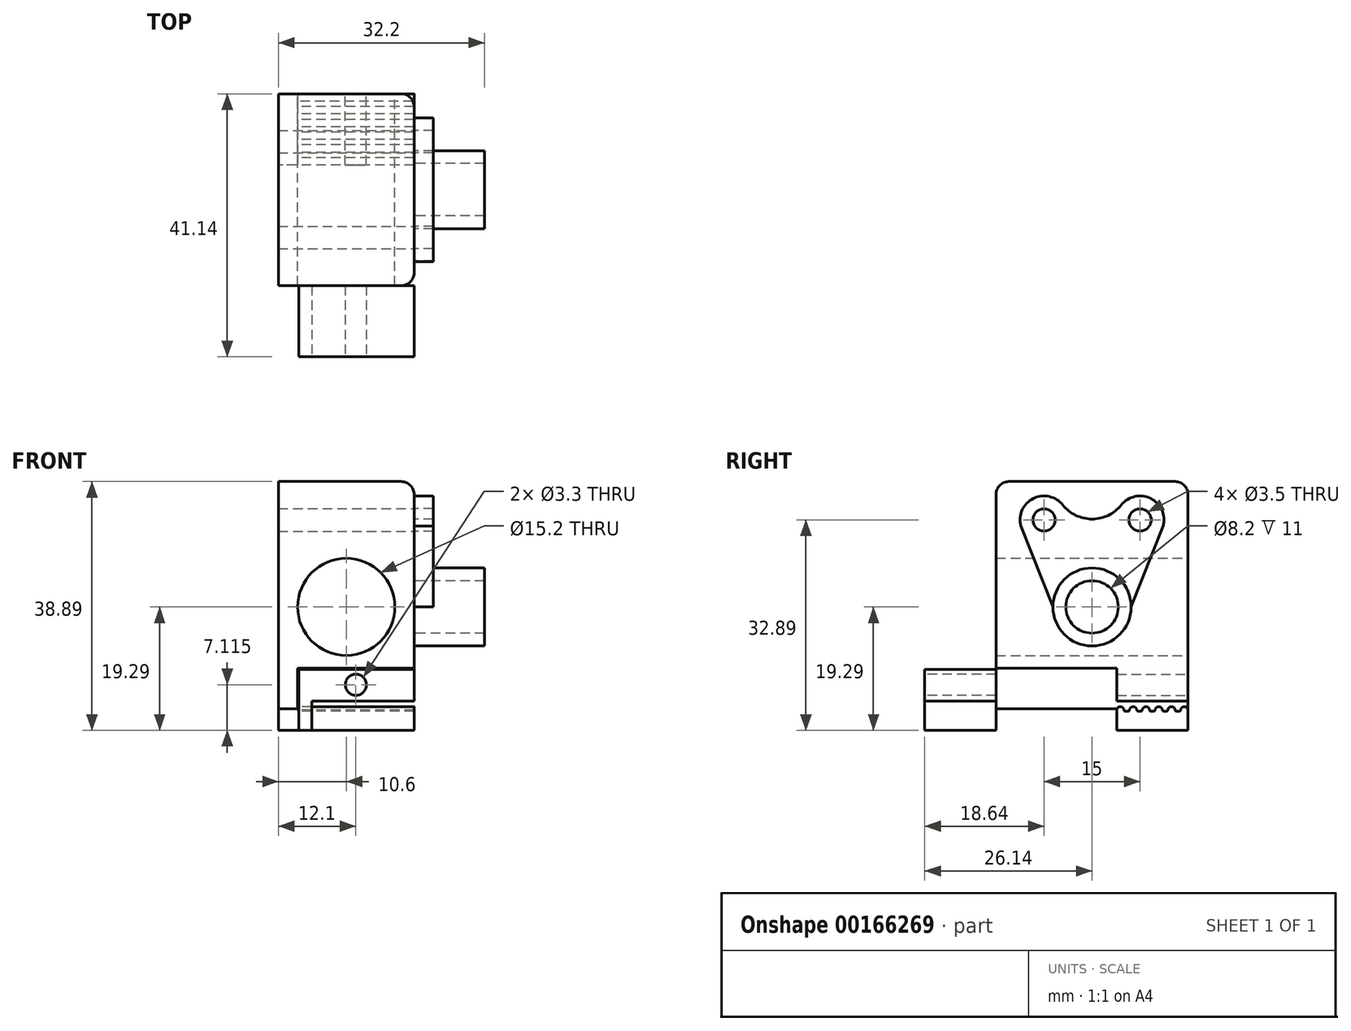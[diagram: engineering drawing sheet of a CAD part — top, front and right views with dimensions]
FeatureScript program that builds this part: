
annotation { "Feature Type Name" : "Feature", "Feature Type Description" : "" }
export const myFeature = defineFeature(function(context is Context, id is Id, definition is map)
    precondition{}
    {
        {
            var Q0;
            Q0=qCreatedBy(makeId("Front.planeOp"),FACE);
            var sketch = newSketch(context, id + "F0", { "sketchPlane" : qUnion([Q0])});
            skCircle(sketch, "E0", {"center": v(0, 0) * mm, "radius": 7.6 * mm});
            skLineSegment(sketch, "E1.bottom", {"start": v(-10.6, 19.6) * mm, "end": v(10.6, 19.6) * mm});
            skLineSegment(sketch, "E1.top", {"start": v(-10.6, -15.9) * mm, "end": v(-7.6, -15.9) * mm});
            skLineSegment(sketch, "E1.left", {"start": v(-10.6, 19.6) * mm, "end": v(-10.6, -15.9) * mm});
            skLineSegment(sketch, "E1.right", {"start": v(10.6, 19.6) * mm, "end": v(10.6, -9.6) * mm});
            skLineSegment(sketch, "E2", {"start": v(0, 0) * mm, "end": v(0, 19.6) * mm, "construction": true});
            skLineSegment(sketch, "E3", {"start": v(10.6, -9.6) * mm, "end": v(-7.6, -9.6) * mm});
            skLineSegment(sketch, "E4", {"start": v(-7.6, -9.6) * mm, "end": v(-7.6, -15.9) * mm});
            skLineSegment(sketch, "E5", {"start": v(-4.6, -10.75) * mm, "end": v(-4.6, -14.75) * mm});
            skLineSegment(sketch, "E6", {"start": v(-4.6, -14.75) * mm, "end": v(-7.6, -14.75) * mm});
            skLineSegment(sketch, "E7", {"start": v(-7.6, -12.75) * mm, "end": v(-10.6, -12.75) * mm, "construction": true});
            skLineSegment(sketch, "E8.MirrorCS", {"start": v(-4.6, -10.75) * mm, "end": v(-7.6, -10.75) * mm});
            skSolve(sketch);
        }
        {
            var Q0;
            Q0 = qSketchRegion(id + "F0", true);
            extrude(context, id + "F1", {"entities" : qUnion([Q0]), "depth" : 30 * mm});
        }
        {
            var Q0;
            {var subQ0=sQuery(id+"F0.wireOp",EDGE,"E4");Q0=makeQuery(id+"F1.opExtrude","SWEPT_FACE",FACE,{"disambiguationData":[OSD([subQ0]),TDD([makeQuery(id+"F0.imprint","IMPRINT",EDGE,{"disambiguationData":[TD([[makeQuery(id+"F0.imprint","INTERSECT",VERTEX,{"derivedFrom":[sQuery(id+"F0.wireOp",EDGE,"E3"),subQ0]}),-1.0]])],"derivedFrom":subQ0})])]});}
            var sketch = newSketch(context, id + "F2", { "sketchPlane" : qUnion([Q0])});
            skLineSegment(sketch, "E9.bottom", {"start": v(0, -9.6) * mm, "end": v(-11.14, -9.6) * mm});
            skLineSegment(sketch, "E9.top", {"start": v(-11.14, -12.6) * mm, "end": v(-30, -12.6) * mm, "construction": true});
            skLineSegment(sketch, "E9.left", {"start": v(0, -9.6) * mm, "end": v(0, -15.9) * mm});
            skLineSegment(sketch, "E9.right", {"start": v(-11.14, -9.6) * mm, "end": v(-11.14, -12.6) * mm});
            skLineSegment(sketch, "E10", {"start": v(-8.58, -12.6) * mm, "end": v(-8.58, -11.78) * mm, "construction": true});
            skArc(sketch, "E11", {"start": v(-8.08, -12.84) * mm, "mid": v(-8.58, -13.16) * mm, "end": v(-9.08, -12.84) * mm, "construction": true});
            skArc(sketch, "E12", {"start": v(-9.16, -12.6) * mm, "mid": v(-9.2, -12.5) * mm, "end": v(-9.31, -12.45) * mm, "construction": true});
            skArc(sketch, "E13", {"start": v(-9.08, -12.84) * mm, "mid": v(-9.13, -12.72) * mm, "end": v(-9.16, -12.6) * mm, "construction": true});
            skLineSegment(sketch, "E14", {"start": v(-8.58, -12.4) * mm, "end": v(-8.18, -12.4) * mm, "construction": true});
            skLineSegment(sketch, "E15", {"start": v(-9.58, -12.6) * mm, "end": v(-9.58, -11.78) * mm, "construction": true});
            skArc(sketch, "E16.MirrorCS", {"start": v(-11.14, -12.6) * mm, "mid": v(-10.7, -13.14) * mm, "end": v(-10.08, -12.84) * mm, "construction": true});
            skArc(sketch, "E17.MirrorCS", {"start": v(-10.08, -12.84) * mm, "mid": v(-10.03, -12.72) * mm, "end": v(-10, -12.6) * mm, "construction": true});
            skArc(sketch, "E18.MirrorCS", {"start": v(-10, -12.6) * mm, "mid": v(-9.96, -12.5) * mm, "end": v(-9.85, -12.45) * mm, "construction": true});
            skLineSegment(sketch, "E19", {"start": v(-9.31, -12.45) * mm, "end": v(-9.85, -12.45) * mm, "construction": true});
            skArc(sketch, "E20.MirrorCS", {"start": v(-8.08, -12.84) * mm, "mid": v(-8.03, -12.72) * mm, "end": v(-8, -12.6) * mm, "construction": true});
            skArc(sketch, "E21.MirrorCS", {"start": v(-7.08, -12.84) * mm, "mid": v(-7.13, -12.72) * mm, "end": v(-7.16, -12.6) * mm, "construction": true});
            skArc(sketch, "E22.MirrorCS", {"start": v(-7.16, -12.6) * mm, "mid": v(-7.2, -12.5) * mm, "end": v(-7.31, -12.45) * mm, "construction": true});
            skArc(sketch, "E23.MirrorCS", {"start": v(-8, -12.6) * mm, "mid": v(-7.96, -12.5) * mm, "end": v(-7.85, -12.45) * mm, "construction": true});
            skLineSegment(sketch, "E24.MirrorCS", {"start": v(-7.85, -12.45) * mm, "end": v(-7.31, -12.45) * mm, "construction": true});
            skArc(sketch, "E25.MirrorCS", {"start": v(-6.08, -12.84) * mm, "mid": v(-6.58, -13.16) * mm, "end": v(-7.08, -12.84) * mm, "construction": true});
            skLineSegment(sketch, "E26.0", {"start": v(-6.58, -16.97) * mm, "end": v(-6.58, -11.78) * mm, "construction": true});
            skArc(sketch, "E27.MirrorCS", {"start": v(-4.08, -12.84) * mm, "mid": v(-4.03, -12.72) * mm, "end": v(-4, -12.6) * mm, "construction": true});
            skArc(sketch, "E28.MirrorCS", {"start": v(-4, -12.6) * mm, "mid": v(-3.96, -12.5) * mm, "end": v(-3.85, -12.45) * mm, "construction": true});
            skArc(sketch, "E29.MirrorCS", {"start": v(-3.08, -12.84) * mm, "mid": v(-3.13, -12.72) * mm, "end": v(-3.16, -12.6) * mm, "construction": true});
            skArc(sketch, "E30.MirrorCS", {"start": v(-3.16, -12.6) * mm, "mid": v(-3.2, -12.5) * mm, "end": v(-3.31, -12.45) * mm, "construction": true});
            skArc(sketch, "E31.MirrorCS", {"start": v(-6, -12.6) * mm, "mid": v(-5.96, -12.5) * mm, "end": v(-5.85, -12.45) * mm, "construction": true});
            skArc(sketch, "E32.MirrorCS", {"start": v(-7.08, -12.84) * mm, "mid": v(-6.58, -13.16) * mm, "end": v(-6.08, -12.84) * mm, "construction": true});
            skArc(sketch, "E33.MirrorCS", {"start": v(-5.16, -12.6) * mm, "mid": v(-5.2, -12.5) * mm, "end": v(-5.31, -12.45) * mm, "construction": true});
            skArc(sketch, "E34.MirrorCS", {"start": v(-6.08, -12.84) * mm, "mid": v(-6.03, -12.72) * mm, "end": v(-6, -12.6) * mm, "construction": true});
            skArc(sketch, "E35.MirrorCS", {"start": v(-5.08, -12.84) * mm, "mid": v(-5.13, -12.72) * mm, "end": v(-5.16, -12.6) * mm, "construction": true});
            skArc(sketch, "E36.MirrorCS", {"start": v(-5.08, -12.84) * mm, "mid": v(-4.58, -13.16) * mm, "end": v(-4.08, -12.84) * mm, "construction": true});
            skArc(sketch, "E37.MirrorCS", {"start": v(-2.03, -12.6) * mm, "mid": v(-2.46, -13.14) * mm, "end": v(-3.08, -12.84) * mm, "construction": true});
            skLineSegment(sketch, "E38.MirrorCS", {"start": v(-5.31, -12.45) * mm, "end": v(-5.85, -12.45) * mm, "construction": true});
            skLineSegment(sketch, "E39.MirrorCS", {"start": v(-3.85, -12.45) * mm, "end": v(-3.31, -12.45) * mm, "construction": true});
            skLineSegment(sketch, "E40.MirrorCS", {"start": v(-2.03, -9.6) * mm, "end": v(-2.03, -12.6) * mm, "construction": true});
            skLineSegment(sketch, "E41.0", {"start": v(-2.58, -16.97) * mm, "end": v(-2.58, -11.78) * mm, "construction": true});
            skPoint(sketch, "E42.orphan", {"position": v(-8.03, -12.6) * mm});
            skPoint(sketch, "E43.orphan", {"position": v(-7.14, -12.6) * mm});
            skPoint(sketch, "E44.orphan", {"position": v(-6.03, -12.6) * mm});
            skPoint(sketch, "E45.orphan", {"position": v(-5.14, -12.6) * mm});
            skArc(sketch, "E46.MirrorCS", {"start": v(-2.08, -12.84) * mm, "mid": v(-2.03, -12.72) * mm, "end": v(-2, -12.6) * mm, "construction": true});
            skArc(sketch, "E47.MirrorCS", {"start": v(-2, -12.6) * mm, "mid": v(-1.96, -12.5) * mm, "end": v(-1.85, -12.45) * mm, "construction": true});
            skLineSegment(sketch, "E48.MirrorCS", {"start": v(-1.31, -12.45) * mm, "end": v(-1.85, -12.45) * mm, "construction": true});
            skArc(sketch, "E49.MirrorCS", {"start": v(-1.16, -12.6) * mm, "mid": v(-1.2, -12.5) * mm, "end": v(-1.31, -12.45) * mm, "construction": true});
            skArc(sketch, "E50.MirrorCS", {"start": v(-1.08, -12.84) * mm, "mid": v(-1.13, -12.72) * mm, "end": v(-1.16, -12.6) * mm, "construction": true});
            skArc(sketch, "E51.MirrorCS", {"start": v(-0.08, -12.84) * mm, "mid": v(-0.58, -13.16) * mm, "end": v(-1.08, -12.84) * mm, "construction": true});
            skArc(sketch, "E52.MirrorCS", {"start": v(-0.08, -12.84) * mm, "mid": v(-0.03, -12.72) * mm, "end": v(0, -12.6) * mm, "construction": true});
            skLineSegment(sketch, "E53", {"start": v(0, -12.6) * mm, "end": v(0, -9.6) * mm});
            skLineSegment(sketch, "E54", {"start": v(-2.58, -14.37) * mm, "end": v(-6.58, -14.37) * mm, "construction": true});
            skArc(sketch, "E55.MirrorCS", {"start": v(-2, -16.14) * mm, "mid": v(-1.96, -16.25) * mm, "end": v(-1.85, -16.3) * mm});
            skArc(sketch, "E56.MirrorCS", {"start": v(-7.08, -15.9) * mm, "mid": v(-7.13, -16.02) * mm, "end": v(-7.16, -16.14) * mm});
            skArc(sketch, "E57.MirrorCS", {"start": v(-7.16, -16.14) * mm, "mid": v(-7.2, -16.25) * mm, "end": v(-7.31, -16.3) * mm});
            skArc(sketch, "E58.MirrorCS", {"start": v(-6.08, -15.9) * mm, "mid": v(-6.03, -16.02) * mm, "end": v(-6, -16.14) * mm});
            skArc(sketch, "E59.MirrorCS", {"start": v(-5.16, -16.14) * mm, "mid": v(-5.2, -16.25) * mm, "end": v(-5.31, -16.3) * mm});
            skArc(sketch, "E60.MirrorCS", {"start": v(-6, -16.14) * mm, "mid": v(-5.96, -16.25) * mm, "end": v(-5.85, -16.3) * mm});
            skArc(sketch, "E61.MirrorCS", {"start": v(-8, -16.14) * mm, "mid": v(-7.96, -16.25) * mm, "end": v(-7.85, -16.3) * mm});
            skArc(sketch, "E62.MirrorCS", {"start": v(-10.08, -15.9) * mm, "mid": v(-10.03, -16.02) * mm, "end": v(-10, -16.14) * mm});
            skArc(sketch, "E63.MirrorCS", {"start": v(-10, -16.14) * mm, "mid": v(-9.96, -16.25) * mm, "end": v(-9.85, -16.3) * mm});
            skArc(sketch, "E64.MirrorCS", {"start": v(-9.08, -15.9) * mm, "mid": v(-9.13, -16.02) * mm, "end": v(-9.16, -16.14) * mm});
            skArc(sketch, "E65.MirrorCS", {"start": v(-8.08, -15.9) * mm, "mid": v(-8.03, -16.02) * mm, "end": v(-8, -16.14) * mm});
            skArc(sketch, "E66.MirrorCS", {"start": v(-3.16, -16.14) * mm, "mid": v(-3.2, -16.25) * mm, "end": v(-3.31, -16.3) * mm});
            skArc(sketch, "E67.MirrorCS", {"start": v(-1.08, -15.9) * mm, "mid": v(-1.13, -16.02) * mm, "end": v(-1.16, -16.14) * mm});
            skArc(sketch, "E68.MirrorCS", {"start": v(-5.08, -15.9) * mm, "mid": v(-5.13, -16.02) * mm, "end": v(-5.16, -16.14) * mm});
            skArc(sketch, "E69.MirrorCS", {"start": v(-1.16, -16.14) * mm, "mid": v(-1.2, -16.25) * mm, "end": v(-1.31, -16.3) * mm});
            skArc(sketch, "E70.MirrorCS", {"start": v(-4.08, -15.9) * mm, "mid": v(-4.03, -16.02) * mm, "end": v(-4, -16.14) * mm});
            skArc(sketch, "E71.MirrorCS", {"start": v(-9.16, -16.14) * mm, "mid": v(-9.2, -16.25) * mm, "end": v(-9.31, -16.3) * mm});
            skArc(sketch, "E72.MirrorCS", {"start": v(-3.08, -15.9) * mm, "mid": v(-3.13, -16.02) * mm, "end": v(-3.16, -16.14) * mm});
            skArc(sketch, "E73.MirrorCS", {"start": v(-4, -16.14) * mm, "mid": v(-3.96, -16.25) * mm, "end": v(-3.85, -16.3) * mm});
            skArc(sketch, "E74.MirrorCS", {"start": v(-0.08, -15.9) * mm, "mid": v(-0.03, -16.02) * mm, "end": v(0, -16.14) * mm});
            skLineSegment(sketch, "E75.MirrorCS", {"start": v(-9.31, -16.3) * mm, "end": v(-9.85, -16.3) * mm});
            skArc(sketch, "E76.MirrorCS", {"start": v(-2.08, -15.9) * mm, "mid": v(-2.03, -16.02) * mm, "end": v(-2, -16.14) * mm});
            skArc(sketch, "E77.MirrorCS", {"start": v(-2.03, -16.14) * mm, "mid": v(-2.46, -15.6) * mm, "end": v(-3.08, -15.9) * mm});
            skLineSegment(sketch, "E78.MirrorCS", {"start": v(-7.85, -16.3) * mm, "end": v(-7.31, -16.3) * mm});
            skPoint(sketch, "E79.MirrorP", {"position": v(-6.03, -16.14) * mm});
            skLineSegment(sketch, "E80.MirrorCS", {"start": v(-5.31, -16.3) * mm, "end": v(-5.85, -16.3) * mm});
            skArc(sketch, "E81.MirrorCS", {"start": v(-5.08, -15.9) * mm, "mid": v(-4.58, -15.59) * mm, "end": v(-4.08, -15.9) * mm});
            skPoint(sketch, "E82.MirrorP", {"position": v(-7.14, -16.14) * mm});
            skArc(sketch, "E83.MirrorCS", {"start": v(-8.08, -15.9) * mm, "mid": v(-8.58, -15.59) * mm, "end": v(-9.08, -15.9) * mm});
            skLineSegment(sketch, "E84.MirrorCS", {"start": v(-1.31, -16.3) * mm, "end": v(-1.85, -16.3) * mm});
            skArc(sketch, "E85.MirrorCS", {"start": v(-6.08, -15.9) * mm, "mid": v(-6.58, -15.59) * mm, "end": v(-7.08, -15.9) * mm});
            skPoint(sketch, "E86.MirrorP", {"position": v(-8.03, -16.14) * mm});
            skArc(sketch, "E87.MirrorCS", {"start": v(-7.08, -15.9) * mm, "mid": v(-6.58, -15.59) * mm, "end": v(-6.08, -15.9) * mm});
            skArc(sketch, "E88.MirrorCS", {"start": v(-0.08, -15.9) * mm, "mid": v(-0.58, -15.59) * mm, "end": v(-1.08, -15.9) * mm});
            skArc(sketch, "E89.MirrorCS", {"start": v(-11.14, -16.14) * mm, "mid": v(-10.7, -15.6) * mm, "end": v(-10.08, -15.9) * mm});
            skLineSegment(sketch, "E90.MirrorCS", {"start": v(-3.85, -16.3) * mm, "end": v(-3.31, -16.3) * mm});
            skPoint(sketch, "E91.MirrorP", {"position": v(-5.14, -16.14) * mm});
            skLineSegment(sketch, "E92", {"start": v(-11.14, -16.14) * mm, "end": v(-11.14, -19.3) * mm});
            skLineSegment(sketch, "E93", {"start": v(-11.14, -19.3) * mm, "end": v(0, -19.3) * mm});
            skLineSegment(sketch, "E94", {"start": v(0, -19.3) * mm, "end": v(0, -16.14) * mm});
            skLineSegment(sketch, "E95", {"start": v(0, -12.6) * mm, "end": v(0, -14.09) * mm});
            skLineSegment(sketch, "E96", {"start": v(0, -14.09) * mm, "end": v(-11.14, -14.09) * mm});
            skLineSegment(sketch, "E97", {"start": v(-11.14, -14.09) * mm, "end": v(-11.14, -12.6) * mm});
            skSolve(sketch);
        }
        {
            var Q0;
            {var subQ0=sQuery(id+"F2.wireOp",EDGE,"E9.bottom");Q0=makeQuery(id+"F2.imprint","IMPRINT",FACE,{"disambiguationData":[TD([[makeQuery(id+"F2.imprint","IMPRINT",EDGE,{"derivedFrom":subQ0}),-1.0]])]});}
            var Q1;
            Q1=makeQuery(id+"F2.imprint","IMPRINT",FACE,{"disambiguationData":[TD([[makeQuery(id+"F2.imprint","IMPRINT",EDGE,{"derivedFrom":sQuery(id+"F2.wireOp",EDGE,"E11")}),-1.0]])]});
            var Q2;
            Q2=makeQuery(id+"F1.opExtrude","SWEPT_FACE",FACE,{"disambiguationData":[OSD([sQuery(id+"F0.wireOp",EDGE,"E5")])]});
            var Q3;
            Q3=makeQuery(id+"F2.imprint","IMPRINT",FACE,{"disambiguationData":[TD([[makeQuery(id+"F2.imprint","IMPRINT",EDGE,{"derivedFrom":sQuery(id+"F2.wireOp",EDGE,"E55.MirrorCS")}),-1.0]])]});
            var Q4;
            Q4=makeQuery(id+"F1.opExtrude","SWEPT_FACE",FACE,{"disambiguationData":[OSD([sQuery(id+"F0.wireOp",EDGE,"E1.right")])]});
            extrude(context, id + "F3", {"entities" : qUnion([Q0, Q1, Q2, Q3]), "operationType" : NewBodyOperationType.ADD, "endBound" : BoundingType.UP_TO_SURFACE, "endBoundEntityFace" : qUnion([Q4]), "depth" : 25 * mm});
        }
        {
            var Q0;
            {var subQ0=sQuery(id+"F0.wireOp",EDGE,"E5");Q0=makeQuery(id+"F3.boolean.opBoolean","MERGE",FACE,{"derivedFrom":[makeQuery(id+"F1.opExtrude","CAP_FACE",FACE,{"disambiguationData":[OSD([sQuery(id+"F0.wireOp",EDGE,"E0"),sQuery(id+"F0.wireOp",EDGE,"E1.bottom"),sQuery(id+"F0.wireOp",EDGE,"E1.top"),sQuery(id+"F0.wireOp",EDGE,"E1.left"),sQuery(id+"F0.wireOp",EDGE,"E1.right"),sQuery(id+"F0.wireOp",EDGE,"E3"),sQuery(id+"F0.wireOp",EDGE,"E4"),subQ0,sQuery(id+"F0.wireOp",EDGE,"E6"),sQuery(id+"F0.wireOp",EDGE,"E8.MirrorCS")])],"isStart":true}),makeQuery(id+"F3.opExtrude","SWEPT_FACE",FACE,{"disambiguationData":[OSD([subQ0]),TDD([makeQuery(id+"F1.opExtrude","CAP_EDGE",EDGE,{"disambiguationData":[OSD([subQ0])],"isStart":true})])]}),makeQuery(id+"F3.opExtrude","SWEPT_FACE",FACE,{"disambiguationData":[OSD([sQuery(id+"F2.wireOp",EDGE,"E53")])]})]});}
            var sketch = newSketch(context, id + "F4", { "sketchPlane" : qUnion([Q0])});
            skLineSegment(sketch, "E98.bottom", {"start": v(10.6, -15.9) * mm, "end": v(7.6, -15.9) * mm});
            skLineSegment(sketch, "E98.top", {"start": v(10.6, -19.3) * mm, "end": v(7.6, -19.3) * mm});
            skLineSegment(sketch, "E98.left", {"start": v(10.6, -15.9) * mm, "end": v(10.6, -19.3) * mm});
            skLineSegment(sketch, "E98.right", {"start": v(7.6, -15.9) * mm, "end": v(7.6, -19.3) * mm});
            skSolve(sketch);
        }
        {
            var Q0;
            Q0=makeQuery(id+"F4.imprint","IMPRINT",FACE,{"disambiguationData":[TD([[makeQuery(id+"F4.imprint","IMPRINT",EDGE,{"derivedFrom":sQuery(id+"F4.wireOp",EDGE,"E98.bottom")}),1.0]])]});
            var Q1;
            Q1=makeQuery(id+"F3.opExtrude","SWEPT_FACE",FACE,{"disambiguationData":[OSD([sQuery(id+"F2.wireOp",EDGE,"E9.right")])]});
            extrude(context, id + "F5", {"entities" : qUnion([Q0]), "operationType" : NewBodyOperationType.ADD, "endBound" : BoundingType.UP_TO_SURFACE, "oppositeDirection" : true, "endBoundEntityFace" : qUnion([Q1]), "depth" : 25 * mm});
        }
        {
            var Q0;
            {var subQ0=sQuery(id+"F0.wireOp",EDGE,"E5");Q0=makeQuery(id+"F5.boolean.opBoolean","MERGE",FACE,{"derivedFrom":[makeQuery(id+"F3.opExtrude","SWEPT_FACE",FACE,{"disambiguationData":[OSD([sQuery(id+"F2.wireOp",EDGE,"E94")])]}),makeQuery(id+"F3.boolean.opBoolean","MERGE",FACE,{"derivedFrom":[makeQuery(id+"F1.opExtrude","CAP_FACE",FACE,{"disambiguationData":[OSD([sQuery(id+"F0.wireOp",EDGE,"E0"),sQuery(id+"F0.wireOp",EDGE,"E1.bottom"),sQuery(id+"F0.wireOp",EDGE,"E1.top"),sQuery(id+"F0.wireOp",EDGE,"E1.left"),sQuery(id+"F0.wireOp",EDGE,"E1.right"),sQuery(id+"F0.wireOp",EDGE,"E3"),sQuery(id+"F0.wireOp",EDGE,"E4"),subQ0,sQuery(id+"F0.wireOp",EDGE,"E6"),sQuery(id+"F0.wireOp",EDGE,"E8.MirrorCS")])],"isStart":true}),makeQuery(id+"F3.opExtrude","SWEPT_FACE",FACE,{"disambiguationData":[OSD([subQ0]),TDD([makeQuery(id+"F1.opExtrude","CAP_EDGE",EDGE,{"disambiguationData":[OSD([subQ0])],"isStart":true})])]}),makeQuery(id+"F3.opExtrude","SWEPT_FACE",FACE,{"disambiguationData":[OSD([sQuery(id+"F2.wireOp",EDGE,"E53")])]})]}),makeQuery(id+"F5.opExtrude","CAP_FACE",FACE,{"disambiguationData":[OSD([sQuery(id+"F4.wireOp",EDGE,"E98.bottom"),sQuery(id+"F4.wireOp",EDGE,"E98.top"),sQuery(id+"F4.wireOp",EDGE,"E98.left"),sQuery(id+"F4.wireOp",EDGE,"E98.right")])],"isStart":true})]});}
            var sketch = newSketch(context, id + "F6", { "sketchPlane" : qUnion([Q0])});
            skLineSegment(sketch, "E99.0", {"start": v(-10.6, -9.6) * mm, "end": v(7.6, -9.6) * mm, "construction": true});
            skLineSegment(sketch, "E100", {"start": v(-1.5, -9.6) * mm, "end": v(-1.5, -14.75) * mm, "construction": true});
            skCircle(sketch, "E101", {"center": v(-1.5, -12.18) * mm, "radius": 1.65 * mm});
            skSolve(sketch);
        }
        {
            var Q0;
            Q0=makeQuery(id+"F6.imprint","IMPRINT",FACE,{"disambiguationData":[TD([[makeQuery(id+"F6.imprint","IMPRINT",EDGE,{"derivedFrom":sQuery(id+"F6.wireOp",EDGE,"E101")}),1.0]])]});
            extrude(context, id + "F7", {"entities" : qUnion([Q0]), "operationType" : NewBodyOperationType.REMOVE, "oppositeDirection" : true, "depth" : 25 * mm});
        }
        {
            var Q0;
            Q0=makeQuery(id+"F1.opExtrude","CAP_FACE",FACE,{"disambiguationData":[OSD([sQuery(id+"F0.wireOp",EDGE,"E0"),sQuery(id+"F0.wireOp",EDGE,"E1.bottom"),sQuery(id+"F0.wireOp",EDGE,"E1.top"),sQuery(id+"F0.wireOp",EDGE,"E1.left"),sQuery(id+"F0.wireOp",EDGE,"E1.right"),sQuery(id+"F0.wireOp",EDGE,"E3"),sQuery(id+"F0.wireOp",EDGE,"E4"),sQuery(id+"F0.wireOp",EDGE,"E5"),sQuery(id+"F0.wireOp",EDGE,"E6"),sQuery(id+"F0.wireOp",EDGE,"E8.MirrorCS")])],"isStart":false});
            var sketch = newSketch(context, id + "F8", { "sketchPlane" : qUnion([Q0])});
            skLineSegment(sketch, "E102.bottom", {"start": v(-7.6, -10.75) * mm, "end": v(10.6, -10.75) * mm});
            skLineSegment(sketch, "E102.top", {"start": v(-7.6, -14.75) * mm, "end": v(10.6, -14.75) * mm});
            skLineSegment(sketch, "E102.left", {"start": v(-7.6, -10.75) * mm, "end": v(-7.6, -14.75) * mm});
            skLineSegment(sketch, "E102.right", {"start": v(10.6, -10.75) * mm, "end": v(10.6, -14.75) * mm});
            skSolve(sketch);
        }
        {
            var Q0;
            Q0 = qSketchRegion(id + "F8", true);
            var Q1;
            Q1=makeQuery(id+"F3.opExtrude","SWEPT_FACE",FACE,{"disambiguationData":[OSD([sQuery(id+"F2.wireOp",EDGE,"E9.right")])]});
            extrude(context, id + "F9", {"entities" : qUnion([Q0]), "operationType" : NewBodyOperationType.REMOVE, "endBound" : BoundingType.UP_TO_SURFACE, "oppositeDirection" : true, "endBoundEntityFace" : qUnion([Q1]), "depth" : 25 * mm});
        }
        {
            var Q0;
            Q0=makeQuery(id+"F3.boolean.opBoolean","MERGE",FACE,{"derivedFrom":[makeQuery(id+"F1.opExtrude","SWEPT_FACE",FACE,{"disambiguationData":[OSD([sQuery(id+"F0.wireOp",EDGE,"E1.right")])]}),makeQuery(id+"F3.opExtrude","CAP_FACE",FACE,{"disambiguationData":[OSD([sQuery(id+"F0.wireOp",EDGE,"E5")])],"isStart":false}),makeQuery(id+"F3.opExtrude","CAP_FACE",FACE,{"disambiguationData":[OSD([sQuery(id+"F0.wireOp",EDGE,"E4"),sQuery(id+"F0.wireOp",EDGE,"E8.MirrorCS"),sQuery(id+"F2.wireOp",EDGE,"E9.bottom"),sQuery(id+"F2.wireOp",EDGE,"E9.right"),sQuery(id+"F2.wireOp",EDGE,"E53")])],"isStart":false})]});
            var sketch = newSketch(context, id + "F10", { "sketchPlane" : qUnion([Q0])});
            skLineSegment(sketch, "E103", {"start": v(-20.57, -9.6) * mm, "end": v(-20.57, 19.6) * mm, "construction": true});
            skLineSegment(sketch, "E104", {"start": v(-30, -9.6) * mm, "end": v(-20.57, -9.6) * mm, "construction": true});
            skLineSegment(sketch, "E105.0", {"start": v(-30, -9.8) * mm, "end": v(-20.57, -9.8) * mm, "construction": true});
            skLineSegment(sketch, "E106", {"start": v(-11.14, -9.6) * mm, "end": v(0, -9.6) * mm, "construction": true});
            skLineSegment(sketch, "E107", {"start": v(0, -9.6) * mm, "end": v(0, -14.75) * mm, "construction": true});
            skLineSegment(sketch, "E108.0", {"start": v(-11.14, -9.6) * mm, "end": v(-11.14, -14.75) * mm, "construction": true});
            skLineSegment(sketch, "E109.0", {"start": v(-11.14, -14.75) * mm, "end": v(0, -14.75) * mm, "construction": true});
            skLineSegment(sketch, "E110.0", {"start": v(0, -19.3) * mm, "end": v(0, -16.14) * mm, "construction": true});
            skArc(sketch, "E110.1", {"start": v(-8.08, -15.9) * mm, "mid": v(-8.58, -15.59) * mm, "end": v(-9.08, -15.9) * mm, "construction": true});
            skArc(sketch, "E110.2", {"start": v(-5.08, -15.9) * mm, "mid": v(-4.58, -15.59) * mm, "end": v(-4.08, -15.9) * mm, "construction": true});
            skArc(sketch, "E110.3", {"start": v(-0.08, -15.9) * mm, "mid": v(-0.58, -15.59) * mm, "end": v(-1.08, -15.9) * mm, "construction": true});
            skLineSegment(sketch, "E110.4", {"start": v(-11.14, -16.14) * mm, "end": v(-11.14, -19.3) * mm, "construction": true});
            skArc(sketch, "E110.5", {"start": v(-6.08, -15.9) * mm, "mid": v(-6.03, -16.02) * mm, "end": v(-6, -16.14) * mm, "construction": true});
            skArc(sketch, "E110.6", {"start": v(-1.16, -16.14) * mm, "mid": v(-1.2, -16.25) * mm, "end": v(-1.31, -16.3) * mm, "construction": true});
            skLineSegment(sketch, "E110.7", {"start": v(-3.85, -16.3) * mm, "end": v(-3.31, -16.3) * mm, "construction": true});
            skArc(sketch, "E110.8", {"start": v(-2, -16.14) * mm, "mid": v(-1.96, -16.25) * mm, "end": v(-1.85, -16.3) * mm, "construction": true});
            skArc(sketch, "E110.9", {"start": v(-11.14, -16.14) * mm, "mid": v(-10.7, -15.6) * mm, "end": v(-10.08, -15.9) * mm, "construction": true});
            skArc(sketch, "E110.10", {"start": v(-9.16, -16.14) * mm, "mid": v(-9.2, -16.25) * mm, "end": v(-9.31, -16.3) * mm, "construction": true});
            skArc(sketch, "E110.11", {"start": v(-5.08, -15.9) * mm, "mid": v(-4.58, -15.59) * mm, "end": v(-4.08, -15.9) * mm, "construction": true});
            skArc(sketch, "E110.12", {"start": v(-8.08, -15.9) * mm, "mid": v(-8.03, -16.02) * mm, "end": v(-8, -16.14) * mm, "construction": true});
            skArc(sketch, "E110.13", {"start": v(-10, -16.14) * mm, "mid": v(-9.96, -16.25) * mm, "end": v(-9.85, -16.3) * mm, "construction": true});
            skArc(sketch, "E110.14", {"start": v(-7.08, -15.9) * mm, "mid": v(-7.13, -16.02) * mm, "end": v(-7.16, -16.14) * mm, "construction": true});
            skArc(sketch, "E110.15", {"start": v(-5.16, -16.14) * mm, "mid": v(-5.2, -16.25) * mm, "end": v(-5.31, -16.3) * mm, "construction": true});
            skLineSegment(sketch, "E110.16", {"start": v(-9.31, -16.3) * mm, "end": v(-9.85, -16.3) * mm, "construction": true});
            skArc(sketch, "E110.17", {"start": v(-4.08, -15.9) * mm, "mid": v(-4.03, -16.02) * mm, "end": v(-4, -16.14) * mm, "construction": true});
            skArc(sketch, "E110.18", {"start": v(-2.08, -15.9) * mm, "mid": v(-2.03, -16.02) * mm, "end": v(-2, -16.14) * mm, "construction": true});
            skLineSegment(sketch, "E110.19", {"start": v(-5.31, -16.3) * mm, "end": v(-5.85, -16.3) * mm, "construction": true});
            skArc(sketch, "E110.20", {"start": v(-6, -16.14) * mm, "mid": v(-5.96, -16.25) * mm, "end": v(-5.85, -16.3) * mm, "construction": true});
            skArc(sketch, "E110.21", {"start": v(-9.08, -15.9) * mm, "mid": v(-9.13, -16.02) * mm, "end": v(-9.16, -16.14) * mm, "construction": true});
            skArc(sketch, "E110.22", {"start": v(-3.08, -15.9) * mm, "mid": v(-3.13, -16.02) * mm, "end": v(-3.16, -16.14) * mm, "construction": true});
            skArc(sketch, "E110.23", {"start": v(-5.08, -15.9) * mm, "mid": v(-5.13, -16.02) * mm, "end": v(-5.16, -16.14) * mm, "construction": true});
            skArc(sketch, "E110.24", {"start": v(-0.08, -15.9) * mm, "mid": v(-0.03, -16.02) * mm, "end": v(0, -16.14) * mm, "construction": true});
            skArc(sketch, "E110.26", {"start": v(-10.08, -15.9) * mm, "mid": v(-10.03, -16.02) * mm, "end": v(-10, -16.14) * mm, "construction": true});
            skLineSegment(sketch, "E110.27", {"start": v(-11.14, -19.3) * mm, "end": v(0, -19.3) * mm, "construction": true});
            skArc(sketch, "E110.28", {"start": v(-3.16, -16.14) * mm, "mid": v(-3.2, -16.25) * mm, "end": v(-3.31, -16.3) * mm, "construction": true});
            skLineSegment(sketch, "E110.29", {"start": v(-1.31, -16.3) * mm, "end": v(-1.85, -16.3) * mm, "construction": true});
            skArc(sketch, "E110.30", {"start": v(-1.08, -15.9) * mm, "mid": v(-1.13, -16.02) * mm, "end": v(-1.16, -16.14) * mm, "construction": true});
            skLineSegment(sketch, "E110.31", {"start": v(-7.85, -16.3) * mm, "end": v(-7.31, -16.3) * mm, "construction": true});
            skArc(sketch, "E110.33", {"start": v(-8, -16.14) * mm, "mid": v(-7.96, -16.25) * mm, "end": v(-7.85, -16.3) * mm, "construction": true});
            skArc(sketch, "E110.34", {"start": v(-2.08, -15.9) * mm, "mid": v(-2.58, -15.59) * mm, "end": v(-3.08, -15.9) * mm, "construction": true});
            skArc(sketch, "E110.35", {"start": v(-7.08, -15.9) * mm, "mid": v(-6.58, -15.59) * mm, "end": v(-6.08, -15.9) * mm, "construction": true});
            skArc(sketch, "E110.36", {"start": v(-8.08, -15.9) * mm, "mid": v(-8.58, -15.59) * mm, "end": v(-9.08, -15.9) * mm, "construction": true});
            skArc(sketch, "E110.37", {"start": v(-0.08, -15.9) * mm, "mid": v(-0.58, -15.59) * mm, "end": v(-1.08, -15.9) * mm, "construction": true});
            skArc(sketch, "E110.38", {"start": v(-7.16, -16.14) * mm, "mid": v(-7.2, -16.25) * mm, "end": v(-7.31, -16.3) * mm, "construction": true});
            skArc(sketch, "E110.39", {"start": v(-4, -16.14) * mm, "mid": v(-3.96, -16.25) * mm, "end": v(-3.85, -16.3) * mm, "construction": true});
            skArc(sketch, "E110.40", {"start": v(-2.08, -15.9) * mm, "mid": v(-2.58, -15.59) * mm, "end": v(-3.08, -15.9) * mm, "construction": true});
            skArc(sketch, "E110.41", {"start": v(-7.08, -15.9) * mm, "mid": v(-7.13, -16.02) * mm, "end": v(-7.16, -16.14) * mm, "construction": true});
            skArc(sketch, "E110.45", {"start": v(-2.08, -15.9) * mm, "mid": v(-2.03, -16.02) * mm, "end": v(-2, -16.14) * mm, "construction": true});
            skLineSegment(sketch, "E110.47", {"start": v(-1.31, -16.3) * mm, "end": v(-1.85, -16.3) * mm, "construction": true});
            skArc(sketch, "E110.49", {"start": v(-4.08, -15.9) * mm, "mid": v(-4.03, -16.02) * mm, "end": v(-4, -16.14) * mm, "construction": true});
            skArc(sketch, "E110.53", {"start": v(-11.14, -16.14) * mm, "mid": v(-10.7, -15.6) * mm, "end": v(-10.08, -15.9) * mm, "construction": true});
            skLineSegment(sketch, "E110.56", {"start": v(-11.14, -19.3) * mm, "end": v(-11.14, -15.9) * mm, "construction": true});
            skLineSegment(sketch, "E110.58", {"start": v(-11.14, -16.14) * mm, "end": v(-11.14, -15.9) * mm, "construction": true});
            skLineSegment(sketch, "E110.64", {"start": v(-11.14, -19.3) * mm, "end": v(0, -19.3) * mm, "construction": true});
            skArc(sketch, "E110.67", {"start": v(-3.08, -15.9) * mm, "mid": v(-3.13, -16.02) * mm, "end": v(-3.16, -16.14) * mm, "construction": true});
            skLineSegment(sketch, "E110.74", {"start": v(-5.31, -16.3) * mm, "end": v(-5.85, -16.3) * mm, "construction": true});
            skLineSegment(sketch, "E110.75", {"start": v(-9.31, -16.3) * mm, "end": v(-9.85, -16.3) * mm, "construction": true});
            skArc(sketch, "E110.76", {"start": v(-8.08, -15.9) * mm, "mid": v(-8.03, -16.02) * mm, "end": v(-8, -16.14) * mm, "construction": true});
            skArc(sketch, "E110.86", {"start": v(-7.08, -15.9) * mm, "mid": v(-6.58, -15.59) * mm, "end": v(-6.08, -15.9) * mm, "construction": true});
            skArc(sketch, "E110.87", {"start": v(-0.08, -15.9) * mm, "mid": v(-0.03, -16.02) * mm, "end": v(0, -16.14) * mm, "construction": true});
            skArc(sketch, "E110.89", {"start": v(-5.16, -16.14) * mm, "mid": v(-5.2, -16.25) * mm, "end": v(-5.31, -16.3) * mm, "construction": true});
            skArc(sketch, "E110.90", {"start": v(-9.08, -15.9) * mm, "mid": v(-9.13, -16.02) * mm, "end": v(-9.16, -16.14) * mm, "construction": true});
            skArc(sketch, "E110.91", {"start": v(-7.16, -16.14) * mm, "mid": v(-7.2, -16.25) * mm, "end": v(-7.31, -16.3) * mm, "construction": true});
            skArc(sketch, "E110.92", {"start": v(-6.08, -15.9) * mm, "mid": v(-6.03, -16.02) * mm, "end": v(-6, -16.14) * mm, "construction": true});
            skArc(sketch, "E110.93", {"start": v(-8, -16.14) * mm, "mid": v(-7.96, -16.25) * mm, "end": v(-7.85, -16.3) * mm, "construction": true});
            skArc(sketch, "E110.94", {"start": v(-2, -16.14) * mm, "mid": v(-1.96, -16.25) * mm, "end": v(-1.85, -16.3) * mm, "construction": true});
            skArc(sketch, "E110.95", {"start": v(-10.08, -15.9) * mm, "mid": v(-10.03, -16.02) * mm, "end": v(-10, -16.14) * mm, "construction": true});
            skArc(sketch, "E110.96", {"start": v(-3.16, -16.14) * mm, "mid": v(-3.2, -16.25) * mm, "end": v(-3.31, -16.3) * mm, "construction": true});
            skArc(sketch, "E110.97", {"start": v(-5.08, -15.9) * mm, "mid": v(-5.13, -16.02) * mm, "end": v(-5.16, -16.14) * mm, "construction": true});
            skArc(sketch, "E110.98", {"start": v(-1.16, -16.14) * mm, "mid": v(-1.2, -16.25) * mm, "end": v(-1.31, -16.3) * mm, "construction": true});
            skArc(sketch, "E110.99", {"start": v(-4, -16.14) * mm, "mid": v(-3.96, -16.25) * mm, "end": v(-3.85, -16.3) * mm, "construction": true});
            skLineSegment(sketch, "E110.100", {"start": v(-3.85, -16.3) * mm, "end": v(-3.31, -16.3) * mm, "construction": true});
            skArc(sketch, "E110.101", {"start": v(-6, -16.14) * mm, "mid": v(-5.96, -16.25) * mm, "end": v(-5.85, -16.3) * mm, "construction": true});
            skLineSegment(sketch, "E110.102", {"start": v(-7.85, -16.3) * mm, "end": v(-7.31, -16.3) * mm, "construction": true});
            skArc(sketch, "E110.103", {"start": v(-1.08, -15.9) * mm, "mid": v(-1.13, -16.02) * mm, "end": v(-1.16, -16.14) * mm, "construction": true});
            skArc(sketch, "E110.104", {"start": v(-9.16, -16.14) * mm, "mid": v(-9.2, -16.25) * mm, "end": v(-9.31, -16.3) * mm, "construction": true});
            skArc(sketch, "E110.105", {"start": v(-10, -16.14) * mm, "mid": v(-9.96, -16.25) * mm, "end": v(-9.85, -16.3) * mm, "construction": true});
            skArc(sketch, "E111.MirrorCS", {"start": v(-33.14, -16.14) * mm, "mid": v(-33.18, -16.25) * mm, "end": v(-33.29, -16.3) * mm});
            skArc(sketch, "E112.MirrorCS", {"start": v(-33.97, -16.14) * mm, "mid": v(-33.93, -16.25) * mm, "end": v(-33.82, -16.3) * mm});
            skLineSegment(sketch, "E113.MirrorCS", {"start": v(-37.29, -16.3) * mm, "end": v(-37.82, -16.3) * mm});
            skArc(sketch, "E114.MirrorCS", {"start": v(-34.06, -15.9) * mm, "mid": v(-34, -16.02) * mm, "end": v(-33.97, -16.14) * mm});
            skArc(sketch, "E115.MirrorCS", {"start": v(-31.14, -16.14) * mm, "mid": v(-31.18, -16.25) * mm, "end": v(-31.29, -16.3) * mm});
            skArc(sketch, "E116.MirrorCS", {"start": v(-37.97, -16.14) * mm, "mid": v(-37.93, -16.25) * mm, "end": v(-37.82, -16.3) * mm});
            skArc(sketch, "E117.MirrorCS", {"start": v(-38.06, -15.9) * mm, "mid": v(-38, -16.02) * mm, "end": v(-37.97, -16.14) * mm});
            skArc(sketch, "E118.MirrorCS", {"start": v(-35.97, -16.14) * mm, "mid": v(-35.93, -16.25) * mm, "end": v(-35.82, -16.3) * mm});
            skLineSegment(sketch, "E119.MirrorCS", {"start": v(-33.29, -16.3) * mm, "end": v(-33.82, -16.3) * mm});
            skArc(sketch, "E120.MirrorCS", {"start": v(-32.06, -15.9) * mm, "mid": v(-32, -16.02) * mm, "end": v(-31.97, -16.14) * mm});
            skArc(sketch, "E121.MirrorCS", {"start": v(-35.05, -15.9) * mm, "mid": v(-35.1, -16.02) * mm, "end": v(-35.14, -16.14) * mm});
            skArc(sketch, "E122.MirrorCS", {"start": v(-35.14, -16.14) * mm, "mid": v(-35.18, -16.25) * mm, "end": v(-35.29, -16.3) * mm});
            skArc(sketch, "E123.MirrorCS", {"start": v(-37.05, -15.9) * mm, "mid": v(-37.1, -16.02) * mm, "end": v(-37.14, -16.14) * mm});
            skArc(sketch, "E124.MirrorCS", {"start": v(-39.14, -16.14) * mm, "mid": v(-39.18, -16.25) * mm, "end": v(-39.29, -16.3) * mm});
            skArc(sketch, "E125.MirrorCS", {"start": v(-34.06, -15.9) * mm, "mid": v(-34.55, -15.59) * mm, "end": v(-35.05, -15.9) * mm});
            skLineSegment(sketch, "E126.MirrorCS", {"start": v(-35.82, -16.3) * mm, "end": v(-35.29, -16.3) * mm});
            skArc(sketch, "E127.MirrorCS", {"start": v(-36.06, -15.9) * mm, "mid": v(-36, -16.02) * mm, "end": v(-35.97, -16.14) * mm});
            skArc(sketch, "E128.MirrorCS", {"start": v(-33.05, -15.9) * mm, "mid": v(-32.55, -15.59) * mm, "end": v(-32.06, -15.9) * mm});
            skArc(sketch, "E129.MirrorCS", {"start": v(-31.97, -16.14) * mm, "mid": v(-31.93, -16.25) * mm, "end": v(-31.82, -16.3) * mm});
            skArc(sketch, "E130.MirrorCS", {"start": v(-33.05, -15.9) * mm, "mid": v(-33.1, -16.02) * mm, "end": v(-33.14, -16.14) * mm});
            skArc(sketch, "E131.MirrorCS", {"start": v(-36.06, -15.9) * mm, "mid": v(-36.55, -15.59) * mm, "end": v(-37.05, -15.9) * mm});
            skArc(sketch, "E132.MirrorCS", {"start": v(-37.14, -16.14) * mm, "mid": v(-37.18, -16.25) * mm, "end": v(-37.29, -16.3) * mm});
            skLineSegment(sketch, "E133.MirrorCS", {"start": v(-31.82, -16.3) * mm, "end": v(-31.29, -16.3) * mm});
            skArc(sketch, "E134.MirrorCS", {"start": v(-39.05, -15.9) * mm, "mid": v(-39.1, -16.02) * mm, "end": v(-39.14, -16.14) * mm});
            skArc(sketch, "E135.MirrorCS", {"start": v(-39.05, -15.9) * mm, "mid": v(-38.55, -15.59) * mm, "end": v(-38.06, -15.9) * mm});
            skArc(sketch, "E136.MirrorCS", {"start": v(-39.97, -16.14) * mm, "mid": v(-39.93, -16.25) * mm, "end": v(-39.82, -16.3) * mm});
            skLineSegment(sketch, "E137.MirrorCS", {"start": v(-39.82, -16.3) * mm, "end": v(-39.29, -16.3) * mm});
            skArc(sketch, "E138.MirrorCS", {"start": v(-31.05, -15.9) * mm, "mid": v(-31.1, -16.02) * mm, "end": v(-31.14, -16.14) * mm});
            skArc(sketch, "E139.MirrorCS", {"start": v(-40.06, -15.9) * mm, "mid": v(-40, -16.02) * mm, "end": v(-39.97, -16.14) * mm});
            skLineSegment(sketch, "E140.MirrorCS", {"start": v(-30, -16.14) * mm, "end": v(-30, -15.9) * mm});
            skArc(sketch, "E141.MirrorCS", {"start": v(-30, -16.14) * mm, "mid": v(-30.43, -15.6) * mm, "end": v(-31.05, -15.9) * mm});
            skArc(sketch, "E142.MirrorCS", {"start": v(-41.05, -15.9) * mm, "mid": v(-41.1, -16.02) * mm, "end": v(-41.14, -16.14) * mm});
            skArc(sketch, "E143.MirrorCS", {"start": v(-41.05, -15.9) * mm, "mid": v(-40.55, -15.59) * mm, "end": v(-40.06, -15.9) * mm});
            skLineSegment(sketch, "E144.MirrorCS", {"start": v(-30, -16.14) * mm, "end": v(-30, -19.3) * mm});
            skLineSegment(sketch, "E145.MirrorCS", {"start": v(-30, -19.3) * mm, "end": v(-41.14, -19.3) * mm});
            skLineSegment(sketch, "E146.MirrorCS", {"start": v(-30, -14.75) * mm, "end": v(-41.14, -14.75) * mm});
            skLineSegment(sketch, "E147.MirrorCS", {"start": v(-41.14, -19.3) * mm, "end": v(-41.14, -16.14) * mm});
            skLineSegment(sketch, "E148.MirrorCS", {"start": v(-30, -19.3) * mm, "end": v(-30, -15.9) * mm});
            skLineSegment(sketch, "E149", {"start": v(-30, -14.75) * mm, "end": v(-30, -9.8) * mm});
            skLineSegment(sketch, "E150", {"start": v(-30, -9.8) * mm, "end": v(-41.14, -9.8) * mm});
            skLineSegment(sketch, "E151", {"start": v(-41.14, -9.8) * mm, "end": v(-41.14, -14.75) * mm});
            skSolve(sketch);
        }
        {
            var Q0;
            Q0=makeQuery(id+"F10.imprint","IMPRINT",FACE,{"disambiguationData":[TD([[makeQuery(id+"F10.imprint","IMPRINT",EDGE,{"derivedFrom":sQuery(id+"F10.wireOp",EDGE,"E146.MirrorCS")}),-1.0]])]});
            var Q1;
            Q1=makeQuery(id+"F10.imprint","IMPRINT",FACE,{"disambiguationData":[TD([[makeQuery(id+"F10.imprint","IMPRINT",EDGE,{"derivedFrom":sQuery(id+"F10.wireOp",EDGE,"E114.MirrorCS")}),-1.0]])]});
            extrude(context, id + "F11", {"entities" : qUnion([Q0, Q1]), "oppositeDirection" : true, "depth" : 18 * mm});
        }
        {
            var Q0;
            Q0=makeQuery(id+"F11.opExtrude","SWEPT_FACE",FACE,{"disambiguationData":[OSD([sQuery(id+"F10.wireOp",EDGE,"E151")])]});
            var sketch = newSketch(context, id + "F12", { "sketchPlane" : qUnion([Q0])});
            skCircle(sketch, "E152.0", {"center": v(1.5, -12.18) * mm, "radius": 1.65 * mm});
            skSolve(sketch);
        }
        {
            var Q0;
            Q0 = qSketchRegion(id + "F12", true);
            extrude(context, id + "F13", {"entities" : qUnion([Q0]), "operationType" : NewBodyOperationType.REMOVE, "endBound" : BoundingType.UP_TO_NEXT, "oppositeDirection" : true, "depth" : 25 * mm});
        }
        {
            var Q0;
            Q0=makeQuery(id+"F11.opExtrude","SWEPT_FACE",FACE,{"disambiguationData":[OSD([sQuery(id+"F10.wireOp",EDGE,"E151")])]});
            var sketch = newSketch(context, id + "F14", { "sketchPlane" : qUnion([Q0])});
            skLineSegment(sketch, "E153.bottom", {"start": v(-7.4, -9.8) * mm, "end": v(-5.4, -9.8) * mm});
            skLineSegment(sketch, "E153.top", {"start": v(-7.4, -19.3) * mm, "end": v(-5.4, -19.3) * mm});
            skLineSegment(sketch, "E153.left", {"start": v(-7.4, -9.8) * mm, "end": v(-7.4, -19.3) * mm});
            skLineSegment(sketch, "E153.right", {"start": v(-5.4, -9.8) * mm, "end": v(-5.4, -19.3) * mm});
            skSolve(sketch);
        }
        {
            var Q0;
            {var subQ0=sQuery(id+"F14.wireOp",EDGE,"E153.bottom");Q0=makeQuery(id+"F14.imprint","IMPRINT",FACE,{"disambiguationData":[TD([[makeQuery(id+"F14.imprint","IMPRINT",EDGE,{"derivedFrom":subQ0}),-1.0]])]});}
            var Q1;
            {var subQ0=sQuery(id+"F14.wireOp",EDGE,"E153.top");Q1=makeQuery(id+"F14.imprint","IMPRINT",FACE,{"disambiguationData":[TD([[makeQuery(id+"F14.imprint","IMPRINT",EDGE,{"derivedFrom":subQ0}),1.0]])]});}
            var Q2;
            Q2=makeQuery(id+"F11.opExtrude","SWEPT_FACE",FACE,{"disambiguationData":[OSD([sQuery(id+"F10.wireOp",EDGE,"E149")])]});
            extrude(context, id + "F15", {"entities" : qUnion([Q0, Q1]), "operationType" : NewBodyOperationType.ADD, "endBound" : BoundingType.UP_TO_SURFACE, "oppositeDirection" : true, "endBoundEntityFace" : qUnion([Q2]), "depth" : 25 * mm});
        }
        {
            var Q0;
            Q0=makeQuery(id+"F3.boolean.opBoolean","MERGE",FACE,{"derivedFrom":[makeQuery(id+"F1.opExtrude","SWEPT_FACE",FACE,{"disambiguationData":[OSD([sQuery(id+"F0.wireOp",EDGE,"E1.right")])]}),makeQuery(id+"F3.opExtrude","CAP_FACE",FACE,{"disambiguationData":[OSD([sQuery(id+"F0.wireOp",EDGE,"E5")])],"isStart":false}),makeQuery(id+"F3.opExtrude","CAP_FACE",FACE,{"disambiguationData":[OSD([sQuery(id+"F0.wireOp",EDGE,"E4"),sQuery(id+"F0.wireOp",EDGE,"E8.MirrorCS"),sQuery(id+"F2.wireOp",EDGE,"E9.bottom"),sQuery(id+"F2.wireOp",EDGE,"E9.right"),sQuery(id+"F2.wireOp",EDGE,"E53")])],"isStart":false})]});
            var sketch = newSketch(context, id + "F16", { "sketchPlane" : qUnion([Q0])});
            skLineSegment(sketch, "E154", {"start": v(0, -7.6) * mm, "end": v(-30, -7.6) * mm, "construction": true});
            skLineSegment(sketch, "E155", {"start": v(-30, 7.6) * mm, "end": v(0, 7.6) * mm, "construction": true});
            skLineSegment(sketch, "E156", {"start": v(-15, -7.6) * mm, "end": v(-15, 7.6) * mm, "construction": true});
            skCircle(sketch, "E157", {"center": v(-15, 0) * mm, "radius": 4.1 * mm});
            skArc(sketch, "E158.0", {"start": v(-21.1, 0) * mm, "mid": v(-15, -6.1) * mm, "end": v(-8.9, 0) * mm});
            skLineSegment(sketch, "E159", {"start": v(-15, 7.6) * mm, "end": v(-15, 19.6) * mm, "construction": true});
            skCircle(sketch, "E160", {"center": v(-22.5, 13.6) * mm, "radius": 1.75 * mm});
            skPoint(sketch, "E160.centerSnap0", {"position": v(-15, 13.6) * mm});
            skCircle(sketch, "E161.MirrorC", {"center": v(-7.5, 13.6) * mm, "radius": 1.75 * mm});
            skLineSegment(sketch, "E162", {"start": v(-30, 19.6) * mm, "end": v(-15, 19.6) * mm, "construction": true});
            skPoint(sketch, "E163", {"position": v(-22.5, 19.6) * mm});
            skArc(sketch, "E164.0", {"start": v(-19.57, 15.94) * mm, "mid": v(-24.58, 16.72) * mm, "end": v(-25.78, 11.79) * mm});
            skArc(sketch, "E165.MirrorC", {"start": v(-10.43, 15.94) * mm, "mid": v(-5.82, 16.95) * mm, "end": v(-3.87, 12.66) * mm});
            skLineSegment(sketch, "E166", {"start": v(-3.87, 12.66) * mm, "end": v(-8.9, 0) * mm});
            skArc(sketch, "E167", {"start": v(-19.57, 15.94) * mm, "mid": v(-15, 13.75) * mm, "end": v(-10.43, 15.94) * mm});
            skLineSegment(sketch, "E168.MirrorCS", {"start": v(-26.13, 12.66) * mm, "end": v(-21.1, 0) * mm});
            skSolve(sketch);
        }
        {
            var Q0;
            Q0=makeQuery(id+"F16.imprint","IMPRINT",FACE,{"disambiguationData":[TD([[makeQuery(id+"F16.imprint","IMPRINT",EDGE,{"derivedFrom":sQuery(id+"F16.wireOp",EDGE,"E157")}),-1.0]])]});
            extrude(context, id + "F17", {"entities" : qUnion([Q0]), "depth" : 3 * mm});
        }
        {
            var Q0;
            Q0=makeQuery(id+"F17.opExtrude","CAP_FACE",FACE,{"disambiguationData":[OSD([sQuery(id+"F16.wireOp",EDGE,"E157"),sQuery(id+"F16.wireOp",EDGE,"E158.0"),sQuery(id+"F16.wireOp",EDGE,"E160"),sQuery(id+"F16.wireOp",EDGE,"E161.MirrorC"),sQuery(id+"F16.wireOp",EDGE,"E164.0"),sQuery(id+"F16.wireOp",EDGE,"E165.MirrorC"),sQuery(id+"F16.wireOp",EDGE,"E166"),sQuery(id+"F16.wireOp",EDGE,"E167"),sQuery(id+"F16.wireOp",EDGE,"E168.MirrorCS")])],"isStart":false});
            var sketch = newSketch(context, id + "F18", { "sketchPlane" : qUnion([Q0])});
            skCircle(sketch, "E169.0", {"center": v(-15, 0) * mm, "radius": 4.1 * mm});
            skCircle(sketch, "E170", {"center": v(-15, 0) * mm, "radius": 6.1 * mm});
            skSolve(sketch);
        }
        {
            var Q0;
            Q0=makeQuery(id+"F18.imprint","IMPRINT",FACE,{"disambiguationData":[TD([[makeQuery(id+"F18.imprint","IMPRINT",EDGE,{"derivedFrom":sQuery(id+"F18.wireOp",EDGE,"E169.0")}),-1.0]])]});
            extrude(context, id + "F19", {"entities" : qUnion([Q0]), "operationType" : NewBodyOperationType.ADD, "depth" : 8 * mm});
        }
        {
            var Q0;
            Q0=makeQuery(id+"F3.boolean.opBoolean","MERGE",FACE,{"derivedFrom":[makeQuery(id+"F1.opExtrude","SWEPT_FACE",FACE,{"disambiguationData":[OSD([sQuery(id+"F0.wireOp",EDGE,"E1.right")])]}),makeQuery(id+"F3.opExtrude","CAP_FACE",FACE,{"disambiguationData":[OSD([sQuery(id+"F0.wireOp",EDGE,"E5")])],"isStart":false}),makeQuery(id+"F3.opExtrude","CAP_FACE",FACE,{"disambiguationData":[OSD([sQuery(id+"F0.wireOp",EDGE,"E4"),sQuery(id+"F0.wireOp",EDGE,"E8.MirrorCS"),sQuery(id+"F2.wireOp",EDGE,"E9.bottom"),sQuery(id+"F2.wireOp",EDGE,"E9.right"),sQuery(id+"F2.wireOp",EDGE,"E53")])],"isStart":false})]});
            var sketch = newSketch(context, id + "F20", { "sketchPlane" : qUnion([Q0])});
            skCircle(sketch, "E171.0", {"center": v(-22.5, 13.6) * mm, "radius": 1.75 * mm});
            skCircle(sketch, "E172.0", {"center": v(-7.5, 13.6) * mm, "radius": 1.75 * mm});
            skSolve(sketch);
        }
        {
            var Q0;
            Q0=makeQuery(id+"F20.imprint","IMPRINT",FACE,{"disambiguationData":[TD([[makeQuery(id+"F20.imprint","IMPRINT",EDGE,{"derivedFrom":sQuery(id+"F20.wireOp",EDGE,"E171.0")}),1.0]])]});
            var Q1;
            Q1=makeQuery(id+"F20.imprint","IMPRINT",FACE,{"disambiguationData":[TD([[makeQuery(id+"F20.imprint","IMPRINT",EDGE,{"derivedFrom":sQuery(id+"F20.wireOp",EDGE,"E172.0")}),1.0]])]});
            extrude(context, id + "F21", {"entities" : qUnion([Q0, Q1]), "operationType" : NewBodyOperationType.REMOVE, "endBound" : BoundingType.THROUGH_ALL, "oppositeDirection" : true, "depth" : 25 * mm});
        }
        {
            var Q0;
            Q0=makeQuery(id+"F1.opExtrude","CAP_EDGE",EDGE,{"disambiguationData":[OSD([sQuery(id+"F0.wireOp",EDGE,"E1.bottom")])],"isStart":false});
            var Q1;
            Q1=makeQuery(id+"F1.opExtrude","CAP_EDGE",EDGE,{"disambiguationData":[OSD([sQuery(id+"F0.wireOp",EDGE,"E1.bottom")])],"isStart":true});
            var Q2;
            Q2=makeQuery(id+"F1.opExtrude","SWEPT_EDGE",EDGE,{"disambiguationData":[OSD([sQuery(id+"F0.wireOp",EDGE,"E1.bottom"),sQuery(id+"F0.wireOp",EDGE,"E1.right")])]});
            var Q3;
            Q3=makeQuery(id+"F1.opExtrude","CAP_EDGE",EDGE,{"disambiguationData":[OSD([sQuery(id+"F0.wireOp",EDGE,"E1.right")])],"isStart":false});
            var Q4;
            {var subQ0=sQuery(id+"F0.wireOp",EDGE,"E5");Q4=makeQuery(id+"F3.boolean.opBoolean","MERGE",EDGE,{"derivedFrom":[makeQuery(id+"F1.opExtrude","CAP_EDGE",EDGE,{"disambiguationData":[OSD([sQuery(id+"F0.wireOp",EDGE,"E1.right")])],"isStart":true}),makeQuery(id+"F3.opExtrude","CAP_EDGE",EDGE,{"disambiguationData":[OSD([subQ0]),TDD([makeQuery(id+"F1.opExtrude","CAP_EDGE",EDGE,{"disambiguationData":[OSD([subQ0])],"isStart":true})])],"isStart":false}),makeQuery(id+"F3.opExtrude","CAP_EDGE",EDGE,{"disambiguationData":[OSD([sQuery(id+"F2.wireOp",EDGE,"E53")])],"isStart":false})]});}
            fillet(context, id + "F22", {"entities" : qUnion([Q0, Q1, Q2, Q3, Q4]), "radius" : 2 * mm, "tangentPropagation" : true, "allowEdgeOverflow" : false});
        }
    });
